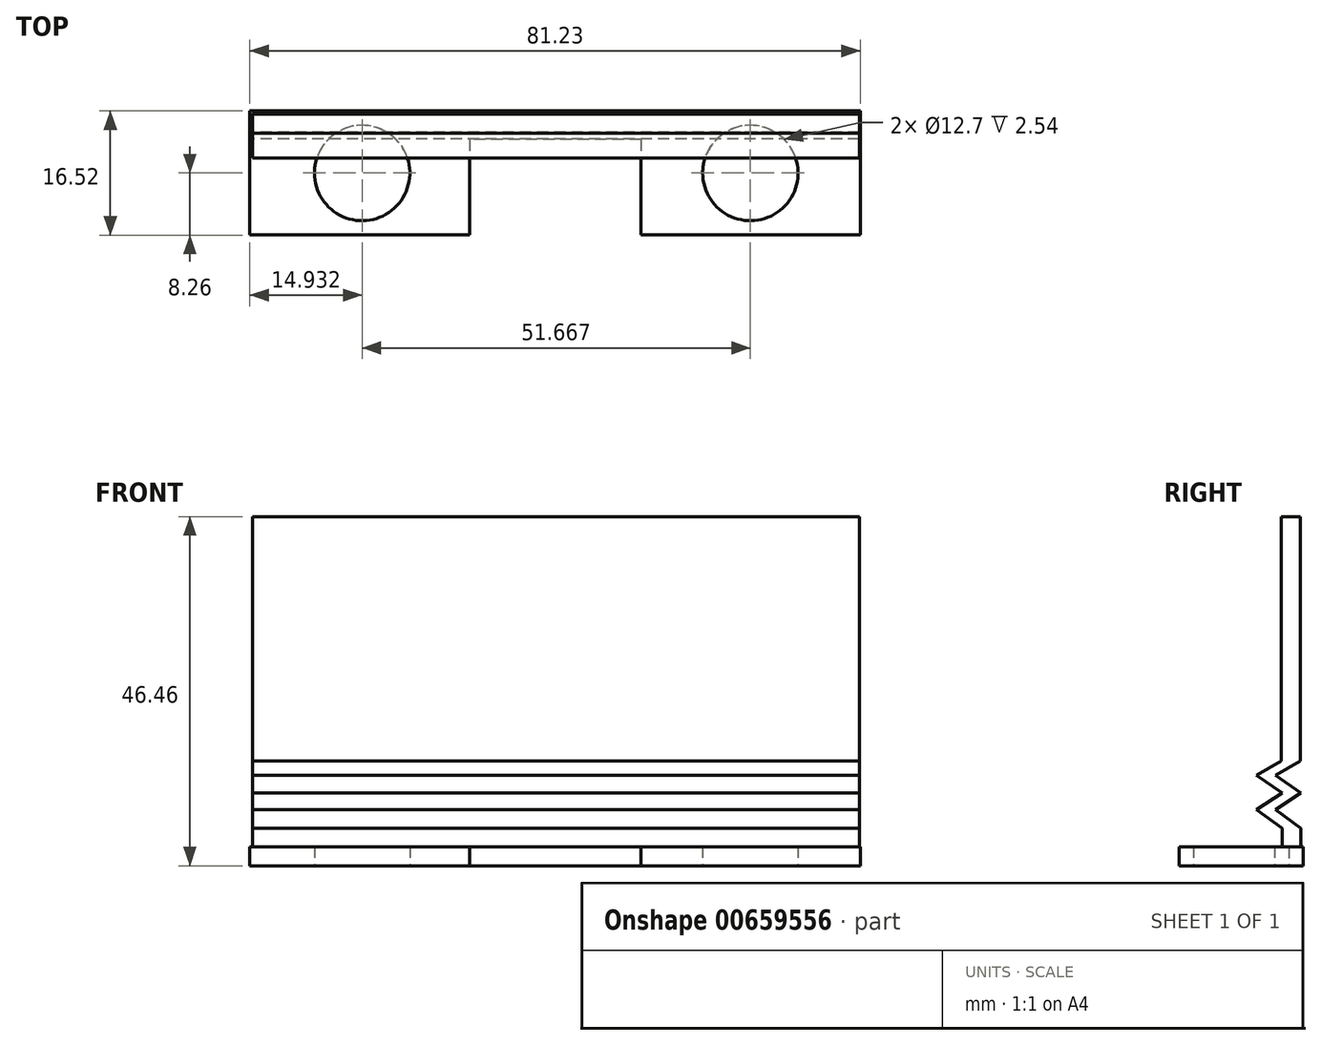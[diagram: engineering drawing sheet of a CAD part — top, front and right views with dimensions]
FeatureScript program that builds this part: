
annotation { "Feature Type Name" : "Feature", "Feature Type Description" : "" }
export const myFeature = defineFeature(function(context is Context, id is Id, definition is map)
    precondition{}
    {
        {
            var Q0;
            Q0=qCreatedBy(makeId("Top.planeOp"),FACE);
            var sketch = newSketch(context, id + "F0", { "sketchPlane" : qUnion([Q0])});
            skPoint(sketch, "E0.middle", {"position": v(-26.62, 0) * mm});
            skPoint(sketch, "E1.middle", {"position": v(25.4, 0) * mm});
            skLineSegment(sketch, "E2.bottom", {"start": v(40, 8.26) * mm, "end": v(10.79, 8.26) * mm});
            skLineSegment(sketch, "E2.top", {"start": v(40, -8.26) * mm, "end": v(10.79, -8.26) * mm});
            skLineSegment(sketch, "E2.left", {"start": v(40, 8.26) * mm, "end": v(40, -8.25) * mm});
            skLineSegment(sketch, "E2.right", {"start": v(10.79, 8.26) * mm, "end": v(10.79, -8.26) * mm});
            skLineSegment(sketch, "E3.bottom", {"start": v(-12.02, 8.26) * mm, "end": v(-41.23, 8.26) * mm});
            skLineSegment(sketch, "E3.top", {"start": v(-12.02, -8.26) * mm, "end": v(-41.23, -8.26) * mm});
            skLineSegment(sketch, "E3.left", {"start": v(-12.02, 8.25) * mm, "end": v(-12.02, -8.26) * mm});
            skLineSegment(sketch, "E3.right", {"start": v(-41.23, 8.26) * mm, "end": v(-41.23, -8.26) * mm});
            skLineSegment(sketch, "E4.bottom", {"start": v(10.79, 8.26) * mm, "end": v(-12.02, 8.26) * mm});
            skLineSegment(sketch, "E4.top", {"start": v(10.79, 4.45) * mm, "end": v(-12.02, 4.44) * mm});
            skLineSegment(sketch, "E4.left", {"start": v(10.79, 8.26) * mm, "end": v(10.79, 4.45) * mm});
            skLineSegment(sketch, "E4.right", {"start": v(-12.02, 8.26) * mm, "end": v(-12.02, 4.44) * mm});
            skSolve(sketch);
        }
        {
            var Q0;
            Q0=makeQuery(id+"F0.imprint","IMPRINT",FACE,{"disambiguationData":[TD([[makeQuery(id+"F0.imprint","IMPRINT",EDGE,{"derivedFrom":sQuery(id+"F0.wireOp",EDGE,"E2.bottom")}),1.0]])]});
            var Q1;
            Q1=makeQuery(id+"F0.imprint","IMPRINT",FACE,{"disambiguationData":[TD([[makeQuery(id+"F0.imprint","IMPRINT",EDGE,{"derivedFrom":sQuery(id+"F0.wireOp",EDGE,"E4.bottom")}),1.0]])]});
            var Q2;
            Q2=makeQuery(id+"F0.imprint","IMPRINT",FACE,{"disambiguationData":[TD([[makeQuery(id+"F0.imprint","IMPRINT",EDGE,{"derivedFrom":sQuery(id+"F0.wireOp",EDGE,"E3.bottom")}),1.0]])]});
            extrude(context, id + "F1", {"entities" : qUnion([Q0, Q1, Q2]), "depth" : 2.54 * mm, "offsetDistance" : 25.4 * mm});
        }
        {
            var Q0;
            Q0=qCreatedBy(makeId("Top.planeOp"),FACE);
            var sketch = newSketch(context, id + "F2", { "sketchPlane" : qUnion([Q0])});
            skLineSegment(sketch, "E5", {"start": v(0, 0) * mm, "end": v(-26.3, 0) * mm});
            skLineSegment(sketch, "E6", {"start": v(0, 0) * mm, "end": v(25.37, 0) * mm});
            skCircle(sketch, "E7", {"center": v(25.37, 0) * mm, "radius": 6.35 * mm});
            skCircle(sketch, "E8", {"center": v(-26.3, 0) * mm, "radius": 6.35 * mm});
            skSolve(sketch);
        }
        {
            var Q0;
            Q0=sQuery(id+"F2.wireOp",VERTEX,"E8.center");
            var Q1;
            Q1=sQuery(id+"F2.wireOp",VERTEX,"E7.center");
            var Q2;
            Q2=makeQuery(id+"F1.opExtrude","SWEPT_BODY",BODY,{"disambiguationData":[OSD([sQuery(id+"F0.wireOp",EDGE,"E2.bottom"),sQuery(id+"F0.wireOp",EDGE,"E2.top"),sQuery(id+"F0.wireOp",EDGE,"E2.left"),sQuery(id+"F0.wireOp",EDGE,"E2.right"),sQuery(id+"F0.wireOp",EDGE,"E3.bottom"),sQuery(id+"F0.wireOp",EDGE,"E3.top"),sQuery(id+"F0.wireOp",EDGE,"E3.left"),sQuery(id+"F0.wireOp",EDGE,"E3.right"),sQuery(id+"F0.wireOp",EDGE,"E4.bottom"),sQuery(id+"F0.wireOp",EDGE,"E4.top")])]});
            hole(context, id + "F3", {"style" : HoleStyle.SIMPLE, "endStyle" : HoleEndStyle.THROUGH, "oppositeDirection" : true, "holeDiameter" : 12.7 * mm, "majorDiameter" : 6.35 * mm, "isTappedThrough" : true, "tappedDepth" : 12.7 * mm, "tapClearance" : 3, "locations" : qUnion([Q0, Q1]), "scope" : qUnion([Q2])});
        }
        {
            var Q0;
            Q0=qCreatedBy(makeId("Right.planeOp"),FACE);
            var sketch = newSketch(context, id + "F4", { "sketchPlane" : qUnion([Q0])});
            skLineSegment(sketch, "E9", {"start": v(7.83, 13.93) * mm, "end": v(7.83, 46.46) * mm});
            skLineSegment(sketch, "E10.bottom", {"start": v(7.96, 2.5) * mm, "end": v(5.42, 2.5) * mm});
            skLineSegment(sketch, "E10.top", {"start": v(7.96, 5.03) * mm, "end": v(5.42, 5.03) * mm});
            skLineSegment(sketch, "E10.left", {"start": v(7.96, 2.5) * mm, "end": v(7.96, 5.03) * mm});
            skLineSegment(sketch, "E10.right", {"start": v(5.42, 2.5) * mm, "end": v(5.42, 5.03) * mm});
            skLineSegment(sketch, "E11", {"start": v(7.96, 5.03) * mm, "end": v(4.56, 7.46) * mm});
            skLineSegment(sketch, "E12", {"start": v(5.42, 5.03) * mm, "end": v(2.03, 7.46) * mm});
            skLineSegment(sketch, "E13", {"start": v(4.56, 7.46) * mm, "end": v(7.96, 9.7) * mm});
            skLineSegment(sketch, "E14", {"start": v(2.03, 7.46) * mm, "end": v(5.42, 9.7) * mm});
            skLineSegment(sketch, "E15", {"start": v(5.42, 9.7) * mm, "end": v(2.03, 12.02) * mm});
            skLineSegment(sketch, "E16", {"start": v(7.96, 9.7) * mm, "end": v(4.56, 12.02) * mm});
            skLineSegment(sketch, "E17", {"start": v(4.56, 12.02) * mm, "end": v(7.83, 13.93) * mm});
            skLineSegment(sketch, "E18", {"start": v(2.03, 12.02) * mm, "end": v(5.3, 13.93) * mm});
            skLineSegment(sketch, "E19", {"start": v(5.3, 13.93) * mm, "end": v(7.83, 13.93) * mm});
            skLineSegment(sketch, "E20", {"start": v(5.3, 13.93) * mm, "end": v(5.3, 46.46) * mm});
            skLineSegment(sketch, "E21", {"start": v(7.83, 46.46) * mm, "end": v(5.3, 46.46) * mm});
            skSolve(sketch);
        }
        {
            var Q0;
            Q0=makeQuery(id+"F4.imprint","IMPRINT",FACE,{"disambiguationData":[TD([[makeQuery(id+"F4.imprint","IMPRINT",EDGE,{"derivedFrom":sQuery(id+"F4.wireOp",EDGE,"E10.top")}),-1.0]])]});
            var Q1;
            Q1=makeQuery(id+"F4.imprint","IMPRINT",FACE,{"disambiguationData":[TD([[makeQuery(id+"F4.imprint","IMPRINT",EDGE,{"derivedFrom":sQuery(id+"F4.wireOp",EDGE,"E9")}),1.0]])]});
            var Q2;
            Q2=makeQuery(id+"F4.imprint","IMPRINT",FACE,{"disambiguationData":[TD([[makeQuery(id+"F4.imprint","IMPRINT",EDGE,{"derivedFrom":sQuery(id+"F4.wireOp",EDGE,"E10.bottom")}),-1.0]])]});
            extrude(context, id + "F5", {"entities" : qUnion([Q0, Q1, Q2]), "operationType" : NewBodyOperationType.ADD, "depth" : 39.88 * mm, "offsetDistance" : 25.4 * mm});
        }
        {
            var Q0;
            Q0=makeQuery(id+"F5.opExtrude","CAP_FACE",FACE,{"disambiguationData":[OSD([sQuery(id+"F4.wireOp",EDGE,"E9"),sQuery(id+"F4.wireOp",EDGE,"E10.bottom"),sQuery(id+"F4.wireOp",EDGE,"E10.left"),sQuery(id+"F4.wireOp",EDGE,"E10.right"),sQuery(id+"F4.wireOp",EDGE,"E11"),sQuery(id+"F4.wireOp",EDGE,"E12"),sQuery(id+"F4.wireOp",EDGE,"E13"),sQuery(id+"F4.wireOp",EDGE,"E14"),sQuery(id+"F4.wireOp",EDGE,"E15"),sQuery(id+"F4.wireOp",EDGE,"E16"),sQuery(id+"F4.wireOp",EDGE,"E17"),sQuery(id+"F4.wireOp",EDGE,"E18"),sQuery(id+"F4.wireOp",EDGE,"E20"),sQuery(id+"F4.wireOp",EDGE,"E21")])],"isStart":true});
            extrude(context, id + "F6", {"entities" : qUnion([Q0]), "operationType" : NewBodyOperationType.ADD, "depth" : 40.9 * mm, "offsetDistance" : 25.4 * mm});
        }
        {
            var Q0;
            Q0=makeQuery(id+"F6.opExtrude","CAP_FACE",FACE,{"disambiguationData":[OSD([sQuery(id+"F4.wireOp",EDGE,"E9"),sQuery(id+"F4.wireOp",EDGE,"E10.bottom"),sQuery(id+"F4.wireOp",EDGE,"E10.left"),sQuery(id+"F4.wireOp",EDGE,"E10.right"),sQuery(id+"F4.wireOp",EDGE,"E11"),sQuery(id+"F4.wireOp",EDGE,"E12"),sQuery(id+"F4.wireOp",EDGE,"E13"),sQuery(id+"F4.wireOp",EDGE,"E14"),sQuery(id+"F4.wireOp",EDGE,"E15"),sQuery(id+"F4.wireOp",EDGE,"E16"),sQuery(id+"F4.wireOp",EDGE,"E17"),sQuery(id+"F4.wireOp",EDGE,"E18"),sQuery(id+"F4.wireOp",EDGE,"E20"),sQuery(id+"F4.wireOp",EDGE,"E21")])],"isStart":false});
            extrude(context, id + "F7", {"entities" : qUnion([Q0]), "operationType" : NewBodyOperationType.ADD, "oppositeDirection" : true, "depth" : 2.54 * mm, "offsetDistance" : 25.4 * mm});
        }
        {
            var Q0;
            Q0=makeQuery(id+"F5.opExtrude","CAP_FACE",FACE,{"disambiguationData":[OSD([sQuery(id+"F4.wireOp",EDGE,"E9"),sQuery(id+"F4.wireOp",EDGE,"E10.bottom"),sQuery(id+"F4.wireOp",EDGE,"E10.left"),sQuery(id+"F4.wireOp",EDGE,"E10.right"),sQuery(id+"F4.wireOp",EDGE,"E11"),sQuery(id+"F4.wireOp",EDGE,"E12"),sQuery(id+"F4.wireOp",EDGE,"E13"),sQuery(id+"F4.wireOp",EDGE,"E14"),sQuery(id+"F4.wireOp",EDGE,"E15"),sQuery(id+"F4.wireOp",EDGE,"E16"),sQuery(id+"F4.wireOp",EDGE,"E17"),sQuery(id+"F4.wireOp",EDGE,"E18"),sQuery(id+"F4.wireOp",EDGE,"E20"),sQuery(id+"F4.wireOp",EDGE,"E21")])],"isStart":false});
            extrude(context, id + "F8", {"entities" : qUnion([Q0]), "operationType" : NewBodyOperationType.ADD, "oppositeDirection" : true, "depth" : 1.27 * mm, "offsetDistance" : 25.4 * mm});
        }
    });
